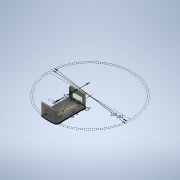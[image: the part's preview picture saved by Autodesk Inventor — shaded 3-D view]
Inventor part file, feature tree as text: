
AUTODESK INVENTOR PART (.ipt)
format: ipt  version: 2020 (Build 240168000, 168)  size: 362,496 bytes
history: native  units: mm
features: projected_geometry x22, extrude x9, sketch x8, other x6
ambient origin geometry x8: Origin, YZ Plane, XZ Plane, XY Plane, X Axis, Y Axis, Z Axis, Center Point
bodies: Body1 (feature_tree)
feature tree (45):
  other  "Твердое тело1"
  sketch  "Эскиз1"
  extrude  "Выдавливание3"  Depth=202.0mm
  other  "РабПлоскость1"
  extrude  "Выдавливание1"  Depth=35.0mm
  other  "РабПлоскость2"
  sketch  "Эскиз2"
  extrude  "Выдавливание4"  Depth=68.0mm
  extrude  "Выдавливание5"  Depth=2.0mm
  sketch  "Эскиз4"
  extrude  "Выдавливание6"  Depth=2.0mm
  extrude  "Выдавливание7"  Depth=3.0mm
  other  "РабПлоскость3"
  extrude  "Выдавливание8"  Depth=3.0mm
  other  "РабПлоскость4"
  extrude  "Выдавливание9"  Depth=210.0mm
  other  "РабПлоскость5"
  extrude  "Выдавливание10"  Depth=20.0mm TaperAngle=0.0deg
  projected_geometry  "Спроецированная петля1"
  projected_geometry  "Спроецированная петля7"
  projected_geometry  "Спроецированная петля8"
  sketch  "Эскиз3"
  projected_geometry  "Спроецированная петля9"
  projected_geometry  "Спроецированная петля10"
  projected_geometry  "Спроецированная петля11"
  projected_geometry  "Спроецированная петля12"
  sketch  "Эскиз5"
  projected_geometry  "Спроецированная петля13"
  projected_geometry  "Спроецированная петля14"
  projected_geometry  "Спроецированная петля15"
  projected_geometry  "Спроецированная петля16"
  projected_geometry  "Спроецированная петля17"
  sketch  "Эскиз6"
  sketch  "Эскиз7"
  projected_geometry  "Спроецированная петля18"
  projected_geometry  "Спроецированная петля19"
  projected_geometry  "Спроецированная петля20"
  projected_geometry  "Спроецированная петля21"
  projected_geometry  "Спроецированная петля22"
  projected_geometry  "Спроецированная петля23"
  projected_geometry  "Спроецированная петля24"
  sketch  "Эскиз8"
  projected_geometry  "Спроецированная петля25"
  projected_geometry  "Спроецированная петля26"
  projected_geometry  "Спроецированная петля27"
